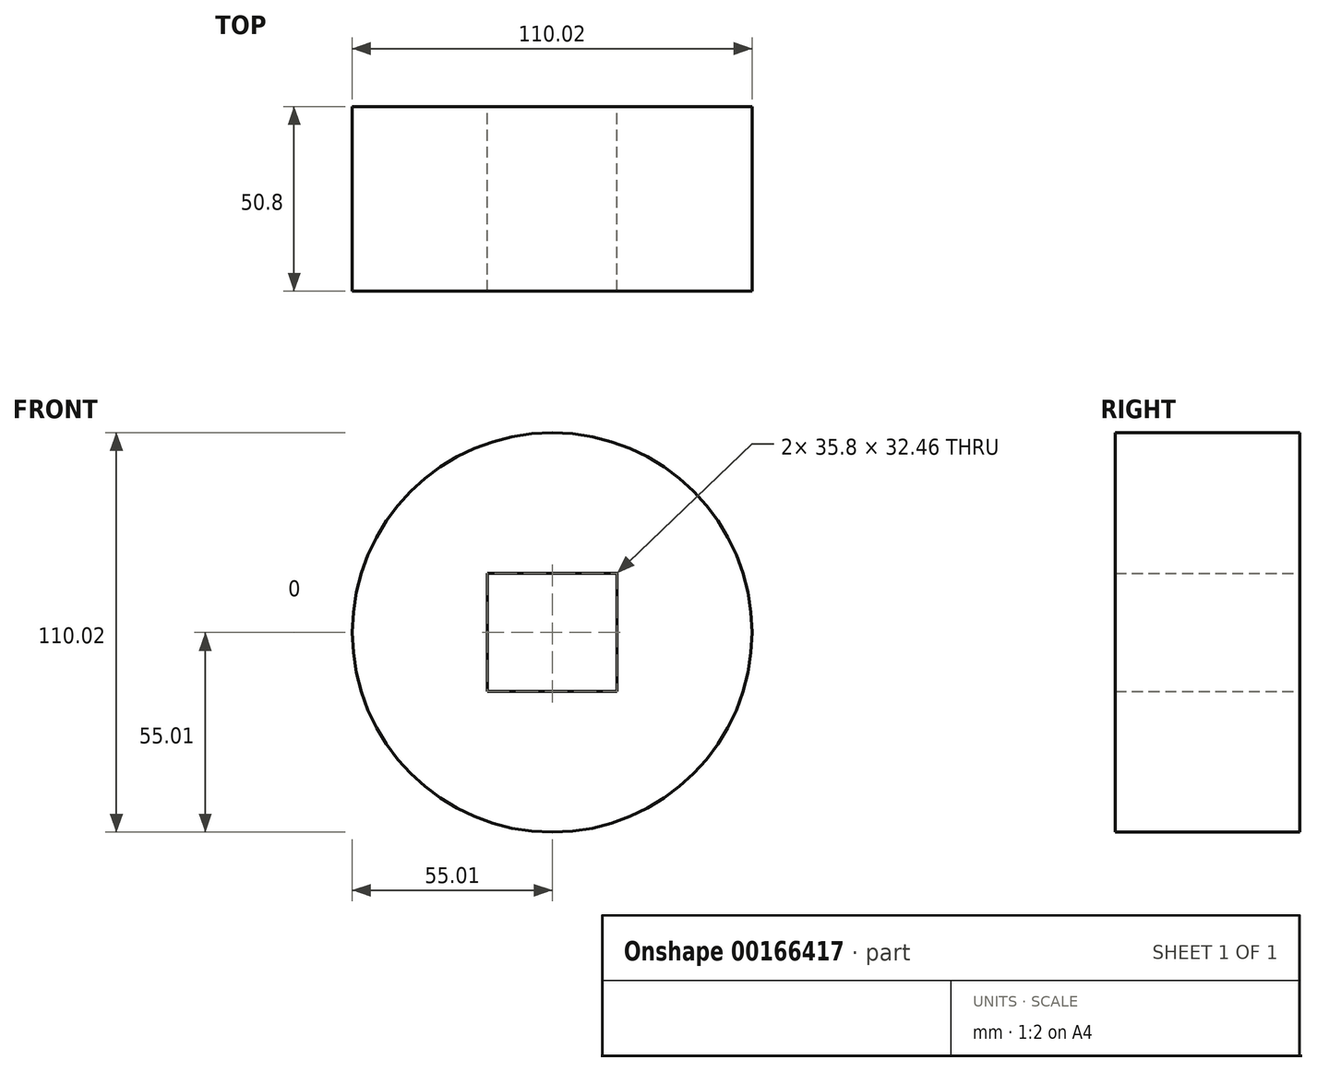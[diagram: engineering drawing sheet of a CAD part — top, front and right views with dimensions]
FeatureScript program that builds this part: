
annotation { "Feature Type Name" : "Feature", "Feature Type Description" : "" }
export const myFeature = defineFeature(function(context is Context, id is Id, definition is map)
    precondition{}
    {
        {
            var Q0;
            Q0=qCreatedBy(makeId("Front.planeOp"),FACE);
            var sketch = newSketch(context, id + "F0", { "sketchPlane" : qUnion([Q0])});
            skCircle(sketch, "E0", {"center": v(0, 0) * mm, "radius": 55 * mm});
            skLineSegment(sketch, "E1.bottom", {"start": v(-17.9, 16.23) * mm, "end": v(17.9, 16.23) * mm});
            skLineSegment(sketch, "E1.top", {"start": v(-17.9, -16.23) * mm, "end": v(17.9, -16.23) * mm});
            skLineSegment(sketch, "E1.left", {"start": v(-17.9, 16.23) * mm, "end": v(-17.9, -16.23) * mm});
            skLineSegment(sketch, "E1.right", {"start": v(17.9, 16.23) * mm, "end": v(17.9, -16.23) * mm});
            skSolve(sketch);
        }
        {
            var Q0;
            Q0=makeQuery(id+"F0.imprint","IMPRINT",FACE,{"disambiguationData":[TD([[makeQuery(id+"F0.imprint","IMPRINT",EDGE,{"derivedFrom":sQuery(id+"F0.wireOp",EDGE,"E0")}),1.0]])]});
            extrude(context, id + "F1", {"entities" : qUnion([Q0]), "depth" : 50.8 * mm});
        }
    });
